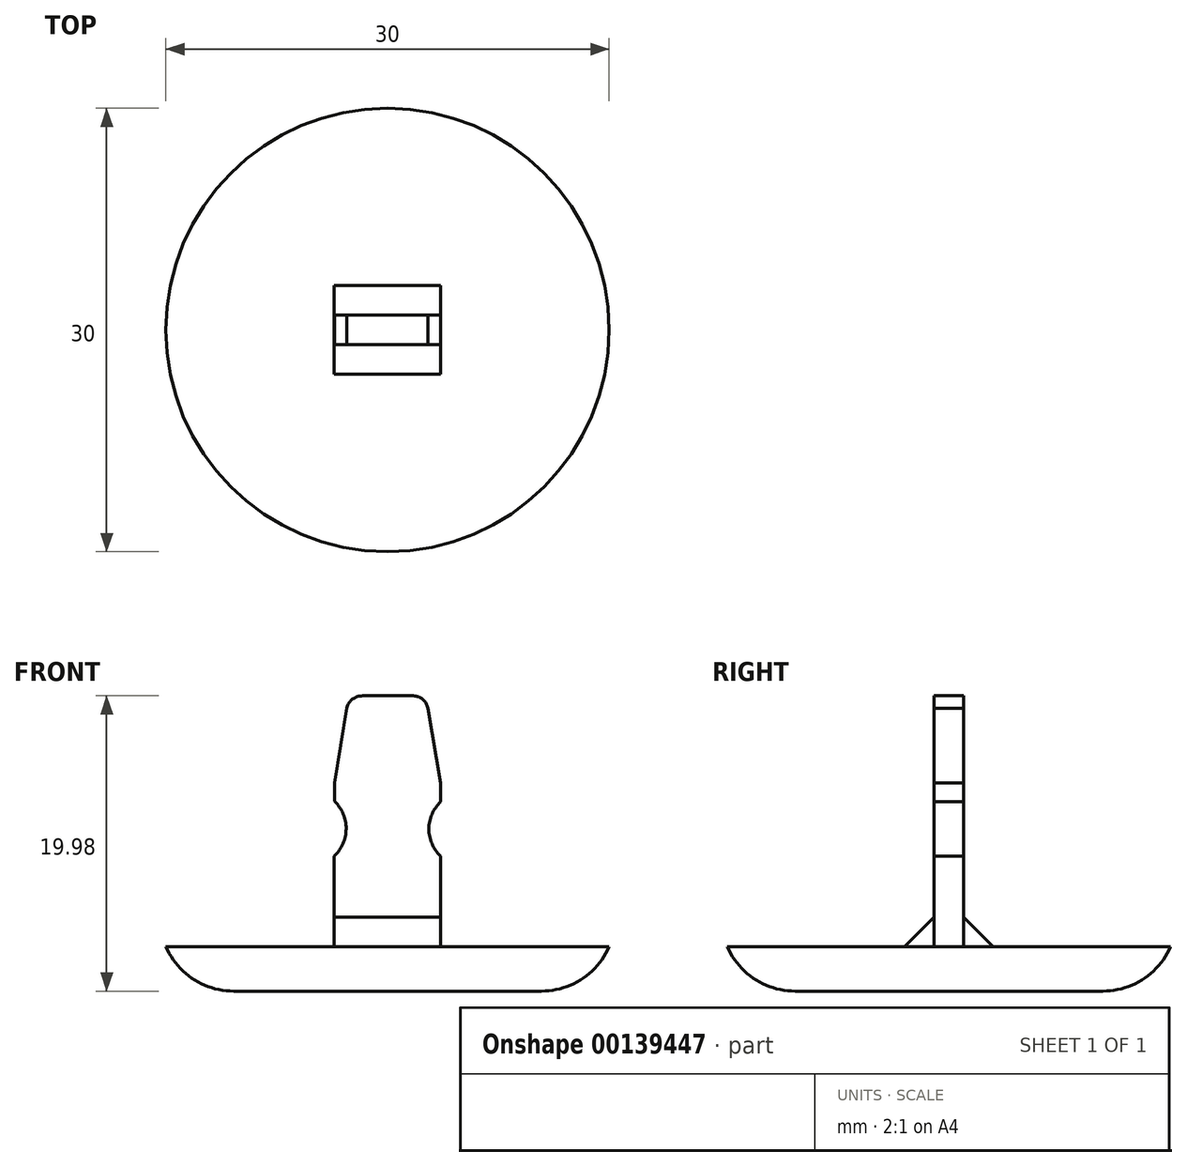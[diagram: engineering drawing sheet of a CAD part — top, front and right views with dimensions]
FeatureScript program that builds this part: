
annotation { "Feature Type Name" : "Feature", "Feature Type Description" : "" }
export const myFeature = defineFeature(function(context is Context, id is Id, definition is map)
    precondition{}
    {
        {
            var Q0;
            Q0=qCreatedBy(makeId("Front.planeOp"),FACE);
            var sketch = newSketch(context, id + "F0", { "sketchPlane" : qUnion([Q0])});
            skLineSegment(sketch, "E0", {"start": v(-2.76, 28) * mm, "end": v(-3.58, 22.9) * mm});
            skLineSegment(sketch, "E1", {"start": v(-3.58, 22.9) * mm, "end": v(-3.58, 21.67) * mm});
            skLineSegment(sketch, "E2", {"start": v(-3.6, 17.97) * mm, "end": v(-3.6, 11.83) * mm});
            skLineSegment(sketch, "E3", {"start": v(-3.6, 11.83) * mm, "end": v(3.6, 11.83) * mm});
            skLineSegment(sketch, "E4", {"start": v(3.6, 11.83) * mm, "end": v(3.6, 17.97) * mm});
            skLineSegment(sketch, "E5", {"start": v(3.6, 21.64) * mm, "end": v(3.6, 22.9) * mm});
            skLineSegment(sketch, "E6", {"start": v(3.6, 22.9) * mm, "end": v(2.73, 27.97) * mm});
            skLineSegment(sketch, "E7", {"start": v(1.76, 28.8) * mm, "end": v(-1.7, 28.8) * mm});
            skArc(sketch, "E8", {"start": v(-1.7, 28.8) * mm, "mid": v(-2.36, 28.58) * mm, "end": v(-2.76, 28) * mm});
            skArc(sketch, "E9", {"start": v(2.73, 27.97) * mm, "mid": v(2.4, 28.57) * mm, "end": v(1.76, 28.8) * mm});
            skArc(sketch, "E10", {"start": v(-3.6, 17.97) * mm, "mid": v(-2.8, 19.81) * mm, "end": v(-3.58, 21.67) * mm});
            skArc(sketch, "E11", {"start": v(3.6, 21.64) * mm, "mid": v(2.8, 19.8) * mm, "end": v(3.6, 17.97) * mm});
            skSolve(sketch);
        }
        {
            var Q0;
            Q0=makeQuery(id+"F0.imprint","IMPRINT",FACE,{"disambiguationData":[TD([[makeQuery(id+"F0.imprint","IMPRINT",EDGE,{"derivedFrom":sQuery(id+"F0.wireOp",EDGE,"E0")}),1.0]])]});
            extrude(context, id + "F1", {"entities" : qUnion([Q0]), "depth" : 2 * mm});
        }
        {
            var Q0;
            Q0=makeQuery(id+"F1.opExtrude","SWEPT_FACE",FACE,{"disambiguationData":[OSD([sQuery(id+"F0.wireOp",EDGE,"E3")])]});
            var sketch = newSketch(context, id + "F2", { "sketchPlane" : qUnion([Q0])});
            skCircle(sketch, "E12", {"center": v(0, 1) * mm, "radius": 15 * mm});
            skSolve(sketch);
        }
        {
            var Q0;
            Q0=makeQuery(id+"F2.imprint","IMPRINT",FACE,{"disambiguationData":[TD([[makeQuery(id+"F2.imprint","IMPRINT",EDGE,{"derivedFrom":sQuery(id+"F2.wireOp",EDGE,"E12")}),1.0]])]});
            var Q1;
            {var subQ0=sQuery(id+"F0.wireOp",EDGE,"E3");Q1=makeQuery(id+"F2.imprint","IMPRINT",FACE,{"disambiguationData":[TD([[makeQuery(id+"F2.imprint","IMPRINT",EDGE,{"derivedFrom":makeQuery(id+"F1.opExtrude","CAP_EDGE",EDGE,{"disambiguationData":[OSD([subQ0])],"isStart":true})}),1.0]])]});}
            extrude(context, id + "F3", {"entities" : qUnion([Q0, Q1]), "depth" : 3 * mm});
        }
        {
            var Q0;
            Q0=makeQuery(id+"F1.opExtrude","CAP_FACE",FACE,{"disambiguationData":[OSD([sQuery(id+"F0.wireOp",EDGE,"E0"),sQuery(id+"F0.wireOp",EDGE,"E1"),sQuery(id+"F0.wireOp",EDGE,"E2"),sQuery(id+"F0.wireOp",EDGE,"E3"),sQuery(id+"F0.wireOp",EDGE,"E4"),sQuery(id+"F0.wireOp",EDGE,"E5"),sQuery(id+"F0.wireOp",EDGE,"E6"),sQuery(id+"F0.wireOp",EDGE,"E7"),sQuery(id+"F0.wireOp",EDGE,"E8"),sQuery(id+"F0.wireOp",EDGE,"E9"),sQuery(id+"F0.wireOp",EDGE,"E10"),sQuery(id+"F0.wireOp",EDGE,"E11")])],"isStart":true});
            var sketch = newSketch(context, id + "F4", { "sketchPlane" : qUnion([Q0])});
            skLineSegment(sketch, "E13.bottom", {"start": v(-3.6, 11.83) * mm, "end": v(3.6, 11.83) * mm});
            skLineSegment(sketch, "E13.top", {"start": v(-3.6, 13.83) * mm, "end": v(3.6, 13.83) * mm});
            skLineSegment(sketch, "E13.left", {"start": v(-3.6, 11.83) * mm, "end": v(-3.6, 13.83) * mm});
            skLineSegment(sketch, "E13.right", {"start": v(3.6, 11.83) * mm, "end": v(3.6, 13.83) * mm});
            skSolve(sketch);
        }
        {
            var Q0;
            Q0=makeQuery(id+"F4.imprint","IMPRINT",FACE,{"disambiguationData":[TD([[makeQuery(id+"F4.imprint","IMPRINT",EDGE,{"derivedFrom":sQuery(id+"F4.wireOp",EDGE,"E13.bottom")}),-1.0]])]});
            extrude(context, id + "F5", {"entities" : qUnion([Q0]), "depth" : 2 * mm});
        }
        {
            var Q0;
            Q0=makeQuery(id+"F5.opExtrude","CAP_EDGE",EDGE,{"disambiguationData":[OSD([sQuery(id+"F4.wireOp",EDGE,"E13.top")])],"isStart":false});
            chamfer(context, id + "F6", {"entities" : qUnion([Q0]), "width" : 2 * mm, "tangentPropagation" : true});
        }
        {
            var Q0;
            Q0=makeQuery(id+"F1.opExtrude","CAP_FACE",FACE,{"disambiguationData":[OSD([sQuery(id+"F0.wireOp",EDGE,"E0"),sQuery(id+"F0.wireOp",EDGE,"E1"),sQuery(id+"F0.wireOp",EDGE,"E2"),sQuery(id+"F0.wireOp",EDGE,"E3"),sQuery(id+"F0.wireOp",EDGE,"E4"),sQuery(id+"F0.wireOp",EDGE,"E5"),sQuery(id+"F0.wireOp",EDGE,"E6"),sQuery(id+"F0.wireOp",EDGE,"E7"),sQuery(id+"F0.wireOp",EDGE,"E8"),sQuery(id+"F0.wireOp",EDGE,"E9"),sQuery(id+"F0.wireOp",EDGE,"E10"),sQuery(id+"F0.wireOp",EDGE,"E11")])],"isStart":false});
            var sketch = newSketch(context, id + "F7", { "sketchPlane" : qUnion([Q0])});
            skLineSegment(sketch, "E14.bottom", {"start": v(-3.6, 11.83) * mm, "end": v(3.6, 11.83) * mm});
            skLineSegment(sketch, "E14.top", {"start": v(-3.6, 13.83) * mm, "end": v(3.6, 13.83) * mm});
            skLineSegment(sketch, "E14.left", {"start": v(-3.6, 11.83) * mm, "end": v(-3.6, 13.83) * mm});
            skLineSegment(sketch, "E14.right", {"start": v(3.6, 11.83) * mm, "end": v(3.6, 13.83) * mm});
            skSolve(sketch);
        }
        {
            var Q0;
            Q0=makeQuery(id+"F7.imprint","IMPRINT",FACE,{"disambiguationData":[TD([[makeQuery(id+"F7.imprint","IMPRINT",EDGE,{"derivedFrom":sQuery(id+"F7.wireOp",EDGE,"E14.bottom")}),1.0]])]});
            extrude(context, id + "F8", {"entities" : qUnion([Q0]), "depth" : 2 * mm});
        }
        {
            var Q0;
            Q0=makeQuery(id+"F8.opExtrude","CAP_EDGE",EDGE,{"disambiguationData":[OSD([sQuery(id+"F7.wireOp",EDGE,"E14.top")])],"isStart":false});
            chamfer(context, id + "F9", {"entities" : qUnion([Q0]), "width" : 2 * mm, "tangentPropagation" : true});
        }
        {
            var Q0;
            Q0=makeQuery(id+"F3.opExtrude","CAP_EDGE",EDGE,{"disambiguationData":[OSD([sQuery(id+"F2.wireOp",EDGE,"E12")])],"isStart":false});
            fillet(context, id + "F10", {"entities" : qUnion([Q0]), "radius" : 5 * mm, "tangentPropagation" : true, "allowEdgeOverflow" : false});
        }
    });
